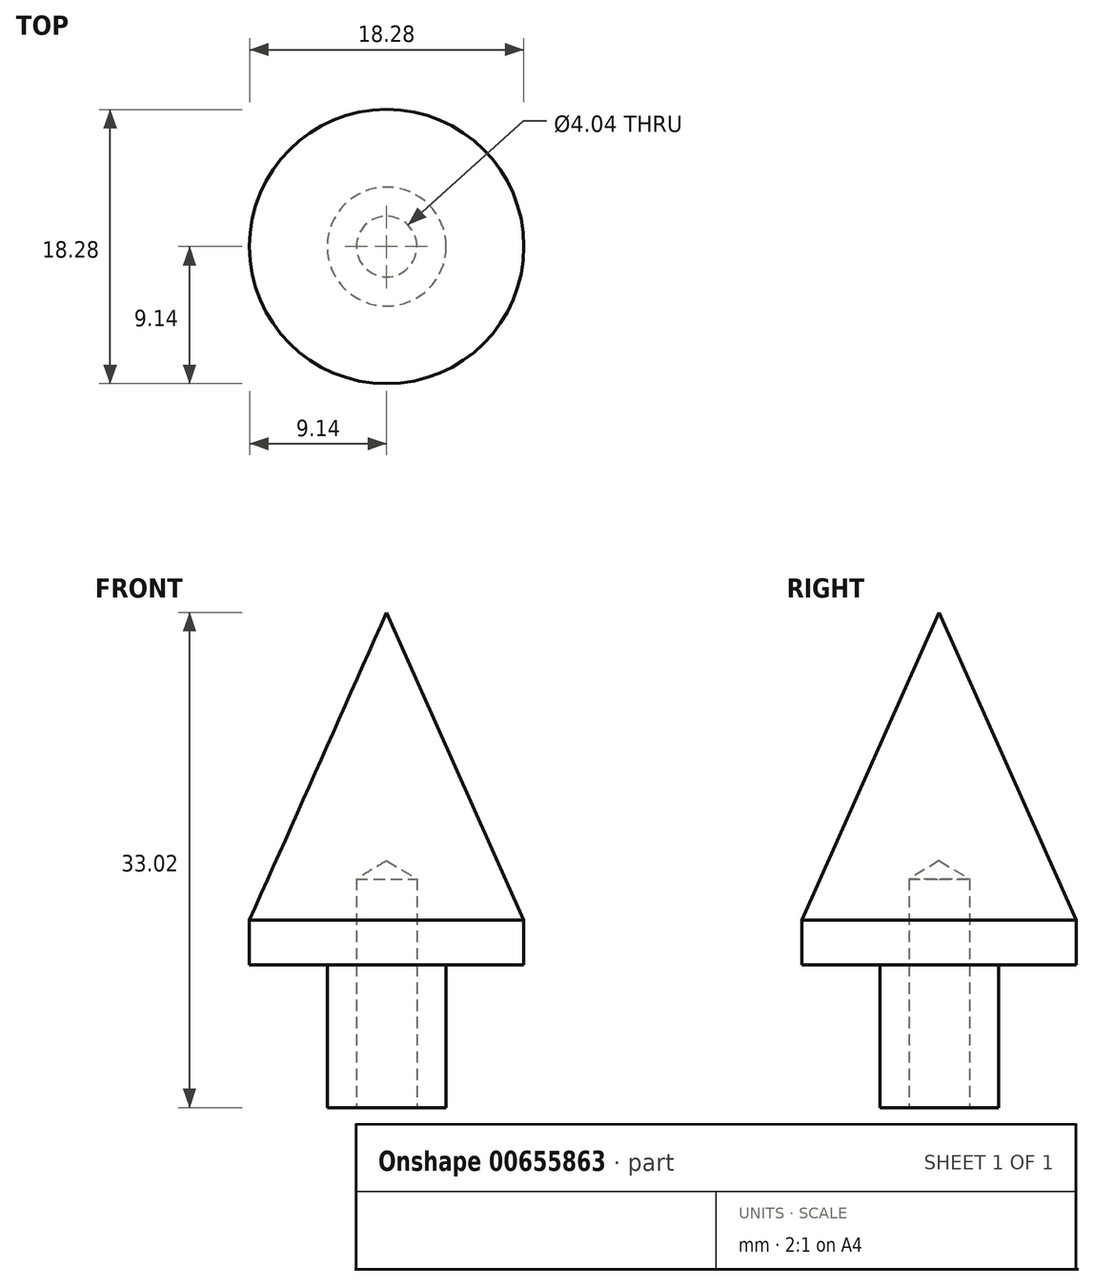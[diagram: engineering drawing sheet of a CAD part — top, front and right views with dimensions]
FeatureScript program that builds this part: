
annotation { "Feature Type Name" : "Feature", "Feature Type Description" : "" }
export const myFeature = defineFeature(function(context is Context, id is Id, definition is map)
    precondition{}
    {
        {
            var Q0;
            Q0=qCreatedBy(makeId("Front.planeOp"),FACE);
            var sketch = newSketch(context, id + "F0", { "sketchPlane" : qUnion([Q0])});
            skLineSegment(sketch, "E0", {"start": v(0, 33.02) * mm, "end": v(-9.14, 12.48) * mm});
            skLineSegment(sketch, "E1", {"start": v(-9.14, 12.48) * mm, "end": v(-9.14, 9.53) * mm});
            skLineSegment(sketch, "E2", {"start": v(-9.14, 9.53) * mm, "end": v(-3.96, 9.53) * mm});
            skLineSegment(sketch, "E3", {"start": v(-3.96, 9.53) * mm, "end": v(-3.96, 0) * mm});
            skLineSegment(sketch, "E4", {"start": v(-3.96, 0) * mm, "end": v(0, 0) * mm});
            skLineSegment(sketch, "E5", {"start": v(0, 0) * mm, "end": v(0, 33.02) * mm});
            skSolve(sketch);
        }
        {
            var Q0;
            Q0 = qSketchRegion(id + "F0", true);
            var Q1;
            Q1=sQuery(id+"F0.wireOp",EDGE,"E5");
            revolve(context, id + "F1", {"entities" : qUnion([Q0]), "axis" : qUnion([Q1]), "revolveType" : RevolveType.FULL});
        }
        {
            var Q0;
            Q0=makeQuery(id+"F1.opRevolve","SWEPT_FACE",FACE,{"disambiguationData":[OSD([sQuery(id+"F0.wireOp",EDGE,"E4")])]});
            var sketch = newSketch(context, id + "F2", { "sketchPlane" : qUnion([Q0])});
            skPoint(sketch, "E6", {"position": v(0, 0) * mm});
            skSolve(sketch);
        }
        {
            var Q0;
            Q0=sQuery(id+"F2.wireOp",VERTEX,"E6");
            var Q1;
            Q1=makeQuery(id+"F1.opRevolve","SWEPT_BODY",BODY,{"disambiguationData":[OSD([sQuery(id+"F0.wireOp",EDGE,"E0"),sQuery(id+"F0.wireOp",EDGE,"E1"),sQuery(id+"F0.wireOp",EDGE,"E2"),sQuery(id+"F0.wireOp",EDGE,"E3"),sQuery(id+"F0.wireOp",EDGE,"E4"),sQuery(id+"F0.wireOp",EDGE,"E5")])]});
            hole(context, id + "F3", {"style" : HoleStyle.SIMPLE, "endStyle" : HoleEndStyle.BLIND, "standardTappedOrClearance" : lookupTablePath({ "standard" : "ANSI", "size" : "#21 (0.16)", "type" : "Drilled" }), "standardBlindInLast" : lookupTablePath({ "standard" : "ANSI", "size" : "#21", "type" : "Drilled" }), "holeDiameter" : 4.04 * mm, "majorDiameter" : 2.84 * mm, "holeDepth" : 15.24 * mm, "tappedDepth" : 12.7 * mm, "tapClearance" : 3, "locations" : qUnion([Q0]), "scope" : qUnion([Q1])});
        }
    });
